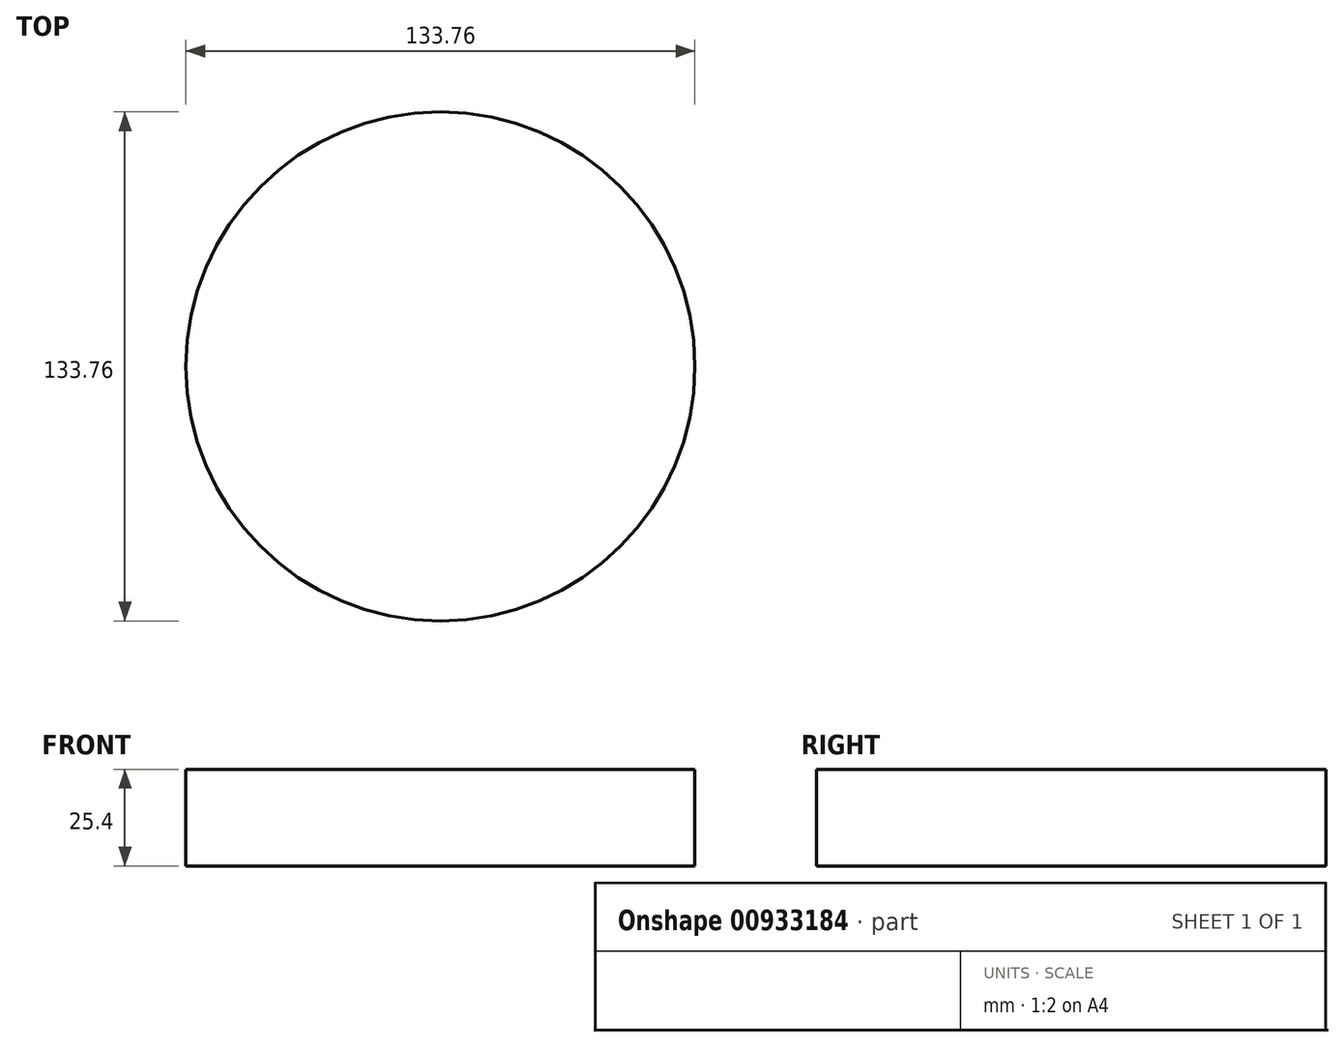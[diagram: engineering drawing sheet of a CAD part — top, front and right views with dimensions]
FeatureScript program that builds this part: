
annotation { "Feature Type Name" : "Feature", "Feature Type Description" : "" }
export const myFeature = defineFeature(function(context is Context, id is Id, definition is map)
    precondition{}
    {
        {
            var Q0;
            Q0=qCreatedBy(makeId("Top.planeOp"),FACE);
            var sketch = newSketch(context, id + "F0", { "sketchPlane" : qUnion([Q0])});
            skCircle(sketch, "E0", {"center": v(0, 0) * mm, "radius": 66.88 * mm});
            skSolve(sketch);
        }
        {
            var Q0;
            Q0=makeQuery(id+"F0.imprint","IMPRINT",FACE,{"disambiguationData":[TD([[makeQuery(id+"F0.imprint","IMPRINT",EDGE,{"derivedFrom":sQuery(id+"F0.wireOp",EDGE,"E0")}),1.0]])]});
            extrude(context, id + "F1", {"entities" : qUnion([Q0]), "depth" : 25.4 * mm, "offsetDistance" : 25.4 * mm});
        }
    });
